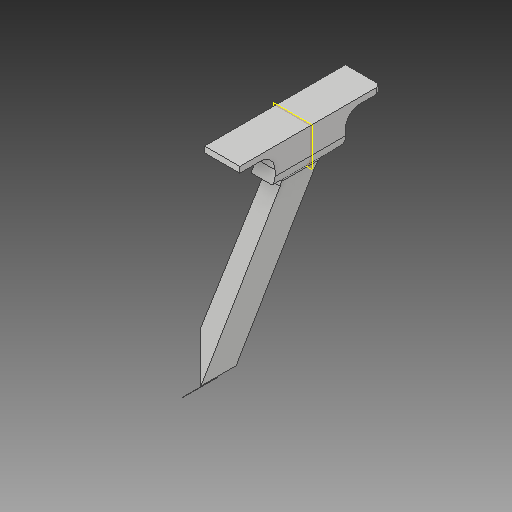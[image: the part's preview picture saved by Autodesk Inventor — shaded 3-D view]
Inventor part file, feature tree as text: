
AUTODESK INVENTOR PART (.ipt)
format: ipt  version: 2018 (Build 220112000, 112)  size: 142,848 bytes
history: native  units: in
note: dims shown in document units (in); Inventor stores cm internally (conversion verified against a paired STEP export)
features: sketch x8, other x3, plane x3
ambient origin geometry x8: Origin, YZ Plane, XZ Plane, XY Plane, X Axis, Y Axis, Z Axis, Center Point
bodies: Solid1 (feature_tree)
feature tree (14):
  other  "bottomARM.ipt"
  other  "Solid1::bottomARM.ipt"
  other  "TaggingFeature1"
  sketch  "Sketch1"  dims[d0=0.3937in]
  sketch  "Sketch3"
  sketch  "Sketch4"
  sketch  "Sketch6"
  sketch  "Sketch7"
  sketch  "Sketch8"
  sketch  "Sketch10"
  sketch  "Sketch11"
  plane  "Work Plane1"
  plane  "Work Plane2"
  plane  "Work Plane3"
